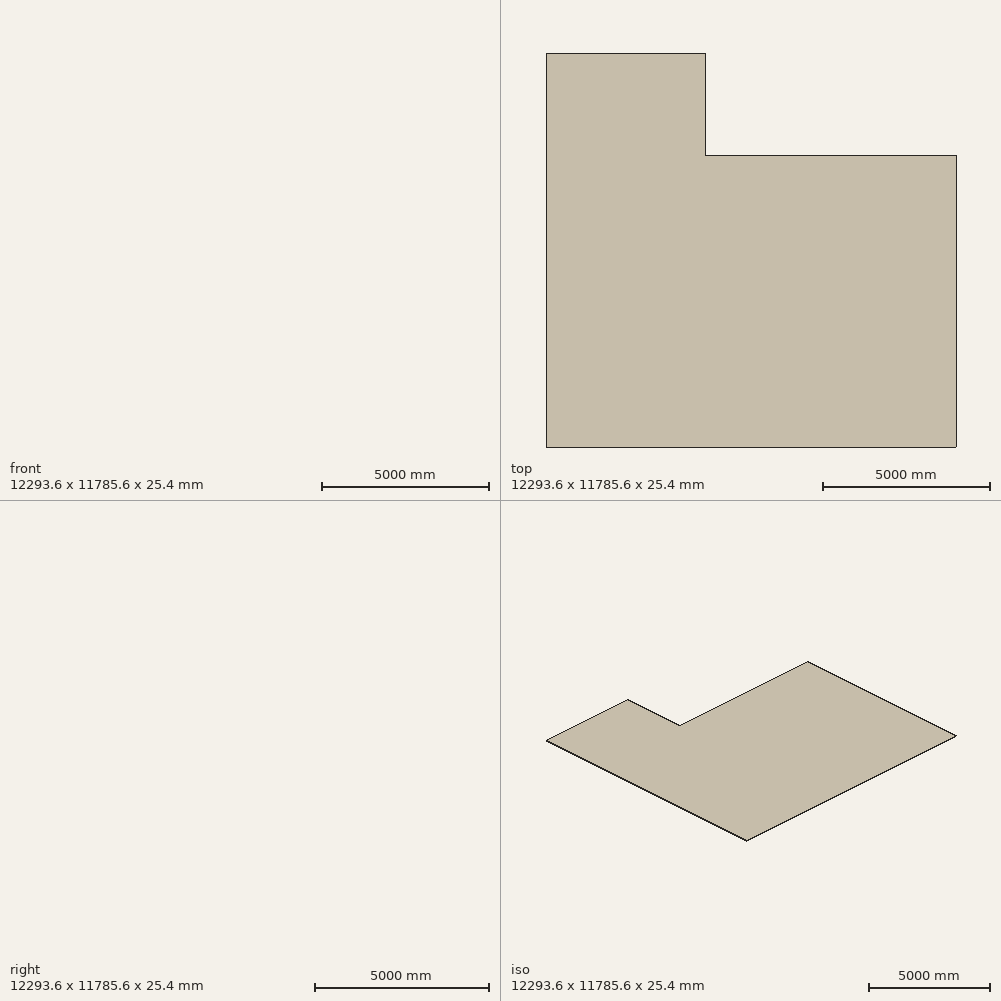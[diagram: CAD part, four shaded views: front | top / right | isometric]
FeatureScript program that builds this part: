
annotation { "Feature Type Name" : "Feature", "Feature Type Description" : "" }
export const myFeature = defineFeature(function(context is Context, id is Id, definition is map)
    precondition{}
    {
        {
            var Q0;
            Q0=qCreatedBy(makeId("Top.planeOp"),FACE);
            var sketch = newSketch(context, id + "F0", { "sketchPlane" : qUnion([Q0])});
            skLineSegment(sketch, "E0.bottom", {"start": v(-6146.8, -4368.8) * mm, "end": v(6146.8, -4368.8) * mm});
            skLineSegment(sketch, "E0.top", {"start": v(-1371.6, 4368.8) * mm, "end": v(6146.8, 4368.8) * mm});
            skLineSegment(sketch, "E0.left", {"start": v(-6146.8, -4368.8) * mm, "end": v(-6146.8, 4368.8) * mm});
            skLineSegment(sketch, "E0.right", {"start": v(6146.8, -4368.8) * mm, "end": v(6146.8, 4368.8) * mm});
            skPoint(sketch, "E0.middle", {"position": v(0, 0) * mm});
            skLineSegment(sketch, "E1", {"start": v(-6146.8, 4368.8) * mm, "end": v(-6146.8, 7416.8) * mm});
            skLineSegment(sketch, "E2", {"start": v(-6146.8, 7416.8) * mm, "end": v(-1371.6, 7416.8) * mm});
            skLineSegment(sketch, "E3", {"start": v(-1371.6, 7416.8) * mm, "end": v(-1371.6, 4368.8) * mm});
            skSolve(sketch);
        }
        {
            var Q0;
            Q0=makeQuery(id+"F0.imprint","IMPRINT",FACE,{"disambiguationData":[TD([[makeQuery(id+"F0.imprint","IMPRINT",EDGE,{"derivedFrom":sQuery(id+"F0.wireOp",EDGE,"E0.bottom")}),1.0]])]});
            extrude(context, id + "F1", {"entities" : qUnion([Q0]), "depth" : 25.4 * mm});
        }
    });
